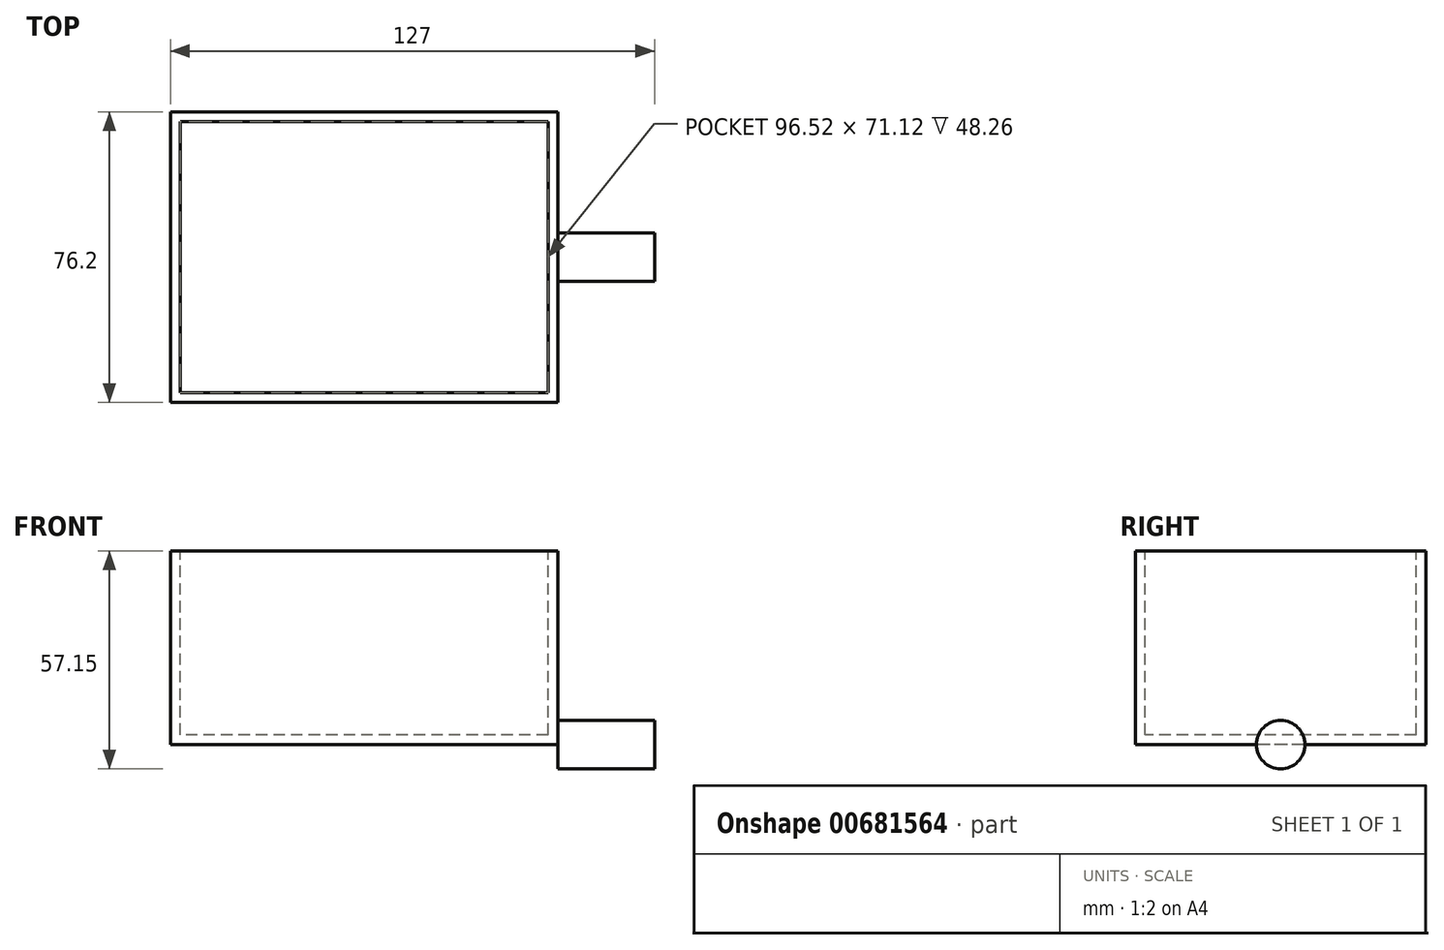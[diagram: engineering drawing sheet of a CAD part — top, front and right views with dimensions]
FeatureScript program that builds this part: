
annotation { "Feature Type Name" : "Feature", "Feature Type Description" : "" }
export const myFeature = defineFeature(function(context is Context, id is Id, definition is map)
    precondition{}
    {
        {
            var Q0;
            Q0=qCreatedBy(makeId("Top.planeOp"),FACE);
            var sketch = newSketch(context, id + "F0", { "sketchPlane" : qUnion([Q0])});
            skLineSegment(sketch, "E0.bottom", {"start": v(50.8, 38.1) * mm, "end": v(-50.8, 38.1) * mm});
            skLineSegment(sketch, "E0.top", {"start": v(50.8, -38.1) * mm, "end": v(-50.8, -38.1) * mm});
            skLineSegment(sketch, "E0.left", {"start": v(50.8, 38.1) * mm, "end": v(50.8, -38.1) * mm});
            skLineSegment(sketch, "E0.right", {"start": v(-50.8, 38.1) * mm, "end": v(-50.8, -38.1) * mm});
            skPoint(sketch, "E0.middle", {"position": v(0, 0) * mm});
            skSolve(sketch);
        }
        {
            var Q0;
            Q0 = qSketchRegion(id + "F0", true);
            extrude(context, id + "F1", {"entities" : qUnion([Q0]), "depth" : 50.8 * mm, "offsetDistance" : 25.4 * mm});
        }
        {
            var Q0;
            Q0=makeQuery(id+"F1.opExtrude","CAP_FACE",FACE,{"disambiguationData":[OSD([sQuery(id+"F0.wireOp",EDGE,"E0.bottom"),sQuery(id+"F0.wireOp",EDGE,"E0.top"),sQuery(id+"F0.wireOp",EDGE,"E0.left"),sQuery(id+"F0.wireOp",EDGE,"E0.right")])],"isStart":false});
            var sketch = newSketch(context, id + "F2", { "sketchPlane" : qUnion([Q0])});
            skPoint(sketch, "E1.0", {"position": v(0, 0) * mm});
            skLineSegment(sketch, "E2.bottom", {"start": v(48.26, 35.56) * mm, "end": v(-48.26, 35.56) * mm});
            skLineSegment(sketch, "E2.top", {"start": v(48.26, -35.56) * mm, "end": v(-48.26, -35.56) * mm});
            skLineSegment(sketch, "E2.left", {"start": v(48.26, 35.56) * mm, "end": v(48.26, -35.56) * mm});
            skLineSegment(sketch, "E2.right", {"start": v(-48.26, 35.56) * mm, "end": v(-48.26, -35.56) * mm});
            skSolve(sketch);
        }
        {
            var Q0;
            Q0=makeQuery(id+"F2.imprint","IMPRINT",FACE,{"disambiguationData":[TD([[makeQuery(id+"F2.imprint","IMPRINT",EDGE,{"derivedFrom":sQuery(id+"F2.wireOp",EDGE,"E2.bottom")}),1.0]])]});
            extrude(context, id + "F3", {"entities" : qUnion([Q0]), "operationType" : NewBodyOperationType.REMOVE, "oppositeDirection" : true, "depth" : 48.26 * mm, "offsetDistance" : 25.4 * mm});
        }
        {
            var Q0;
            Q0=makeQuery(id+"F1.opExtrude","SWEPT_FACE",FACE,{"disambiguationData":[OSD([sQuery(id+"F0.wireOp",EDGE,"E0.left")])]});
            var sketch = newSketch(context, id + "F4", { "sketchPlane" : qUnion([Q0])});
            skCircle(sketch, "E3", {"center": v(0, 0) * mm, "radius": 6.35 * mm});
            skSolve(sketch);
        }
        {
            var Q0;
            Q0 = qSketchRegion(id + "F4", true);
            extrude(context, id + "F5", {"entities" : qUnion([Q0]), "operationType" : NewBodyOperationType.ADD, "depth" : 25.4 * mm, "offsetDistance" : 25.4 * mm});
        }
    });
